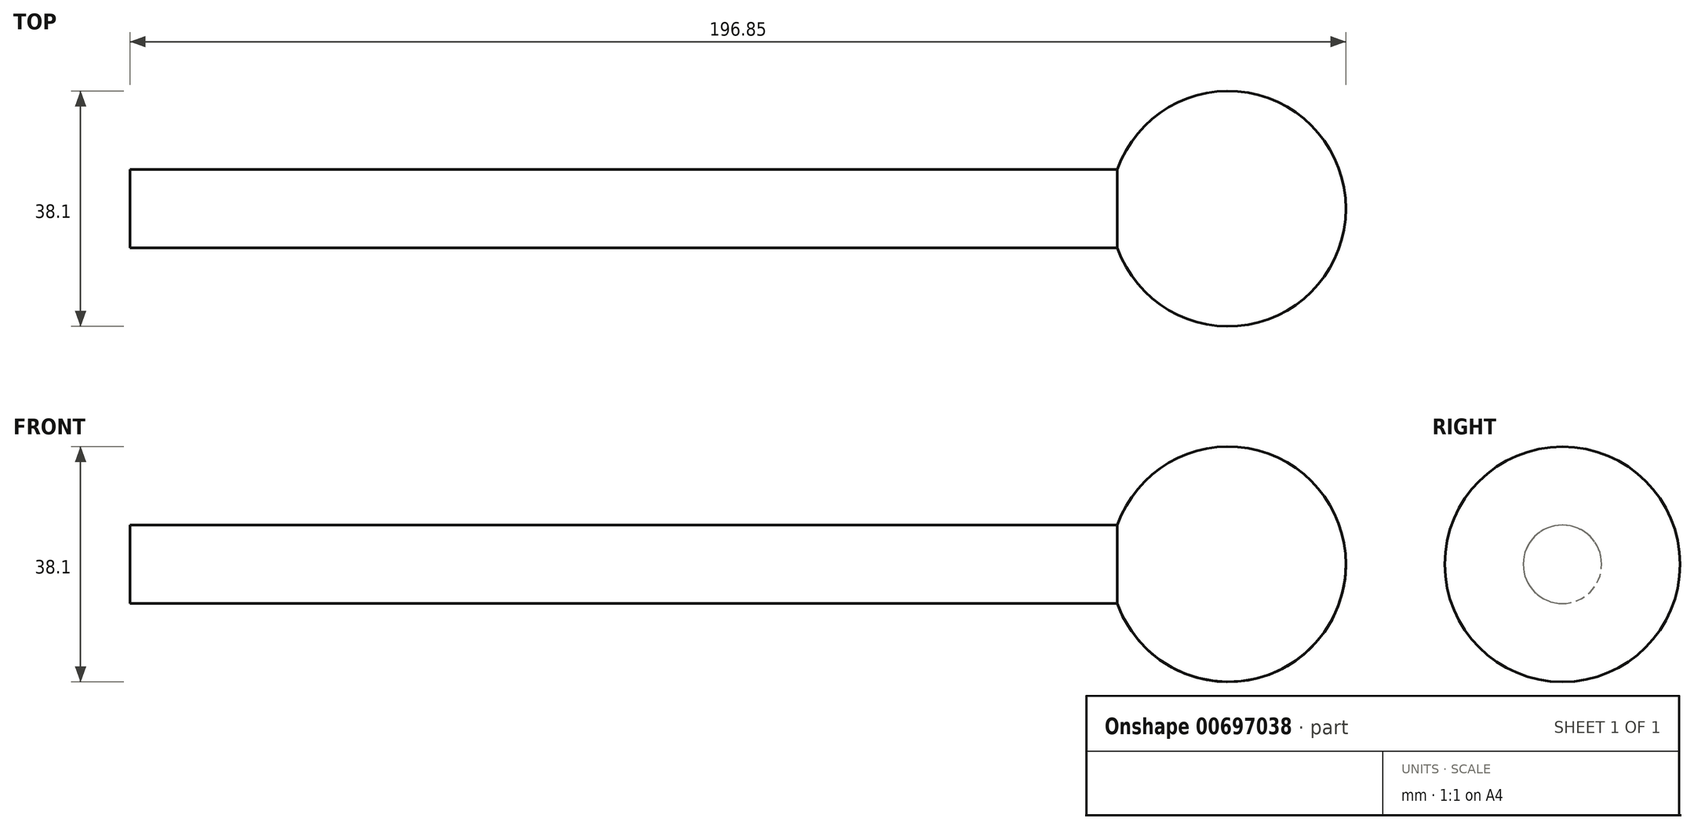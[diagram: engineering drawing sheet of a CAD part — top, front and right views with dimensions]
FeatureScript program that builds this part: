
annotation { "Feature Type Name" : "Feature", "Feature Type Description" : "" }
export const myFeature = defineFeature(function(context is Context, id is Id, definition is map)
    precondition{}
    {
        {
            var Q0;
            Q0=qCreatedBy(makeId("Front.planeOp"),FACE);
            var sketch = newSketch(context, id + "F0", { "sketchPlane" : qUnion([Q0])});
            skLineSegment(sketch, "E0", {"start": v(0, 0) * mm, "end": v(0, 6.35) * mm});
            skLineSegment(sketch, "E1", {"start": v(0, 6.35) * mm, "end": v(159.84, 6.35) * mm});
            skPoint(sketch, "E2", {"position": v(177.8, 0) * mm});
            skArc(sketch, "E3", {"start": v(196.85, 0) * mm, "mid": v(181.02, 18.78) * mm, "end": v(159.84, 6.35) * mm});
            skLineSegment(sketch, "E4", {"start": v(0, 0) * mm, "end": v(196.85, 0) * mm});
            skSolve(sketch);
        }
        {
            var Q0;
            Q0 = qSketchRegion(id + "F0", true);
            var Q1;
            Q1=sQuery(id+"F0.wireOp",EDGE,"E4");
            revolve(context, id + "F1", {"entities" : qUnion([Q0]), "axis" : qUnion([Q1]), "revolveType" : RevolveType.FULL});
        }
    });
